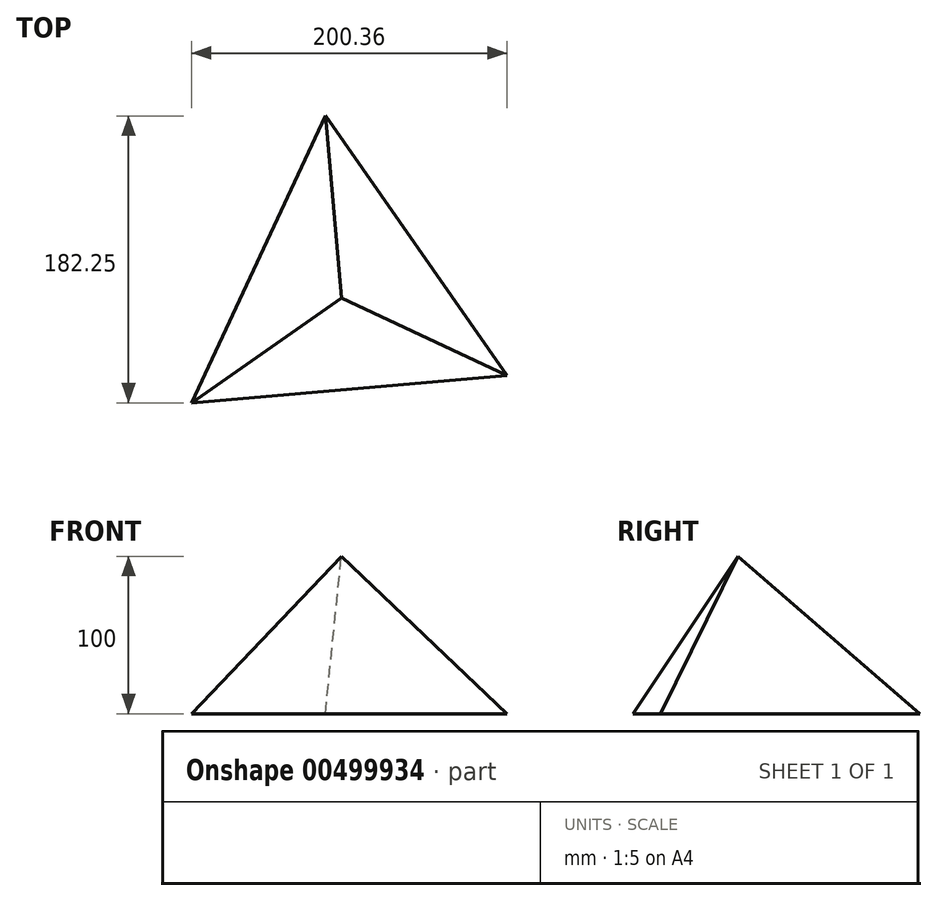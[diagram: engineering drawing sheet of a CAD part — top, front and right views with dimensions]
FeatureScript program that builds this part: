
annotation { "Feature Type Name" : "Feature", "Feature Type Description" : "" }
export const myFeature = defineFeature(function(context is Context, id is Id, definition is map)
    precondition{}
    {
        {
            var Q0;
            Q0=qCreatedBy(makeId("Top.planeOp"),FACE);
            var sketch = newSketch(context, id + "F0", { "sketchPlane" : qUnion([Q0])});
            skCircle(sketch, "E0.cCircle", {"center": v(0, 0) * mm, "radius": 116.12 * mm, "construction": true});
            skLineSegment(sketch, "E0.0", {"start": v(105.22, -49.11) * mm, "end": v(-95.14, -66.57) * mm});
            skLineSegment(sketch, "E0.1", {"start": v(-95.14, -66.57) * mm, "end": v(-10.08, 115.68) * mm});
            skLineSegment(sketch, "E0.2", {"start": v(-10.08, 115.68) * mm, "end": v(105.22, -49.11) * mm});
            skSolve(sketch);
        }
        {
            var Q0;
            Q0=qCreatedBy(makeId("Top.planeOp"),FACE);
            cPlane(context, id + "F1", {"entities" : qUnion([Q0]), "cplaneType" : CPlaneType.OFFSET, "offset" : 100 * mm, "width" : 152.4 * mm, "height" : 152.4 * mm});
        }
        {
            var Q0;
            Q0=qCreatedBy(id+"F1.planeOp",FACE);
            var sketch = newSketch(context, id + "F2", { "sketchPlane" : qUnion([Q0])});
            skPoint(sketch, "E1", {"position": v(0, 0) * mm});
            skSolve(sketch);
        }
        {
            var Q0;
            Q0=makeQuery(id+"F0.imprint","IMPRINT",FACE,{"disambiguationData":[TD([[makeQuery(id+"F0.imprint","IMPRINT",EDGE,{"derivedFrom":sQuery(id+"F0.wireOp",EDGE,"E0.0")}),-1.0]])]});
            var Q1;
            Q1=sQuery(id+"F2.wireOp",VERTEX,"E1");
            loft(context, id + "F3", {"sheetProfilesArray" : [{ "sheetProfileEntities" : qUnion([Q0]) }, { "sheetProfileEntities" : qUnion([Q1]) }]});
        }
    });
